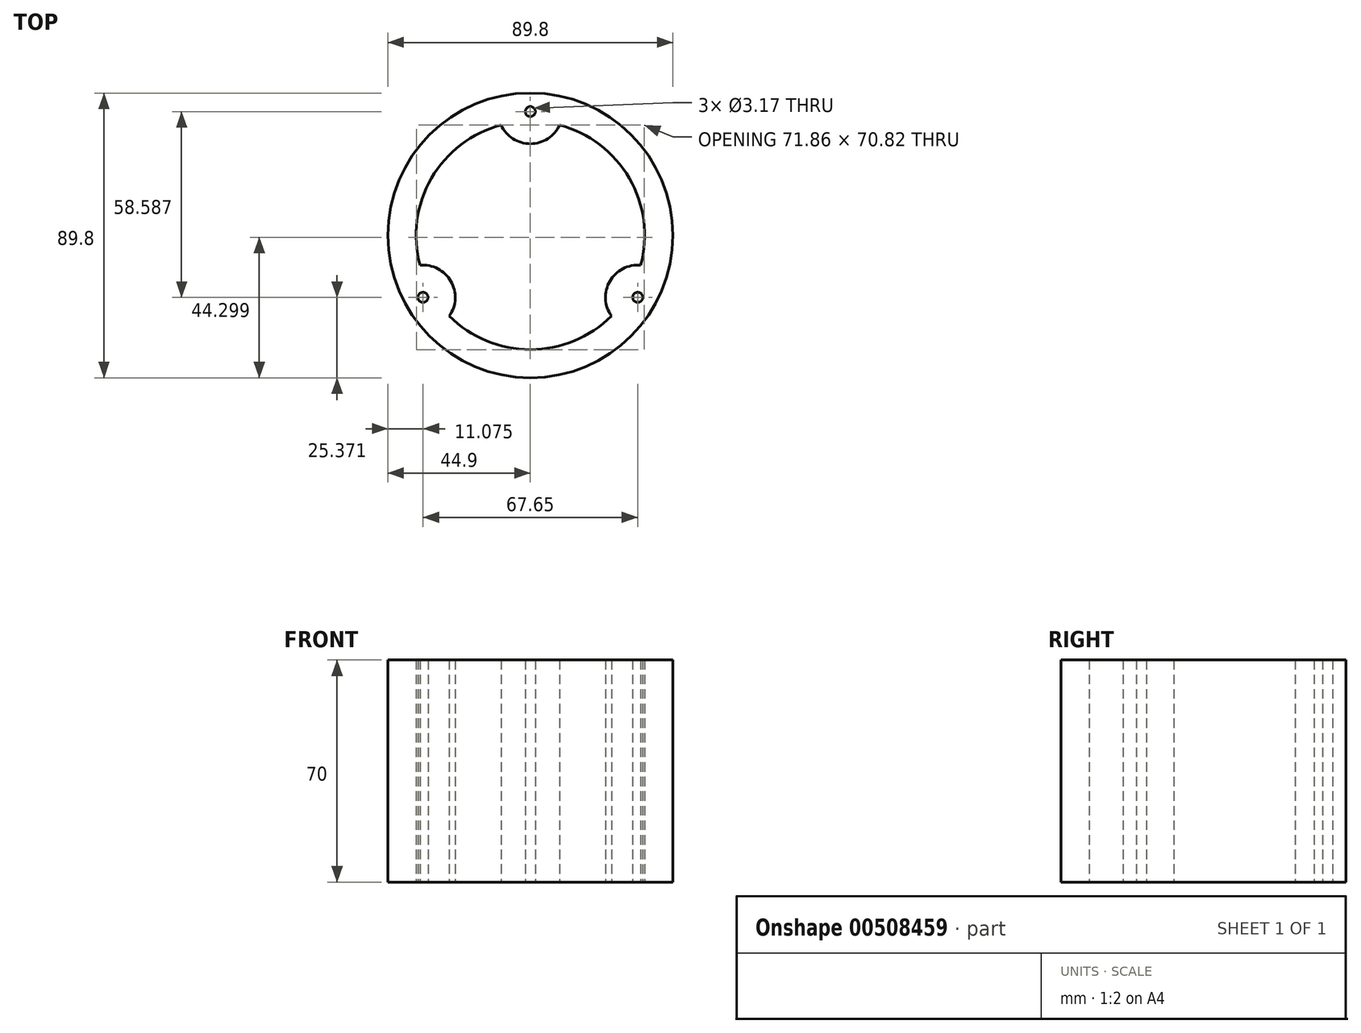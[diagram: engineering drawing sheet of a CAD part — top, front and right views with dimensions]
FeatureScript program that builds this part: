
annotation { "Feature Type Name" : "Feature", "Feature Type Description" : "" }
export const myFeature = defineFeature(function(context is Context, id is Id, definition is map)
    precondition{}
    {
        {
            var Q0;
            Q0=qCreatedBy(makeId("Top.planeOp"),FACE);
            var sketch = newSketch(context, id + "F0", { "sketchPlane" : qUnion([Q0])});
            skCircle(sketch, "E0", {"center": v(0, 0) * mm, "radius": 44.9 * mm});
            skCircle(sketch, "E1", {"center": v(0, 0) * mm, "radius": 36 * mm});
            skPoint(sketch, "E2", {"position": v(0, 39.06) * mm});
            skPoint(sketch, "E3.1.0", {"position": v(-33.83, -19.53) * mm});
            skPoint(sketch, "E3.2.0", {"position": v(33.83, -19.53) * mm});
            skCircle(sketch, "E4", {"center": v(0, 39.06) * mm, "radius": 1.59 * mm});
            skCircle(sketch, "E5", {"center": v(33.83, -19.53) * mm, "radius": 1.59 * mm});
            skCircle(sketch, "E6", {"center": v(-33.83, -19.53) * mm, "radius": 1.59 * mm});
            skCircle(sketch, "E7", {"center": v(0, 39.06) * mm, "radius": 10.16 * mm});
            skCircle(sketch, "E8.1.0", {"center": v(-33.83, -19.53) * mm, "radius": 10.16 * mm});
            skCircle(sketch, "E8.2.0", {"center": v(33.83, -19.53) * mm, "radius": 10.16 * mm});
            skSolve(sketch);
        }
        {
            var Q0;
            Q0=makeQuery(id+"F0.imprint","IMPRINT",FACE,{"disambiguationData":[TD([[makeQuery(id+"F0.imprint","IMPRINT",EDGE,{"derivedFrom":sQuery(id+"F0.wireOp",EDGE,"E6")}),-1.0]])]});
            var Q1;
            {var subQ0=sQuery(id+"F0.wireOp",EDGE,"E8.1.0");var subQ1=sQuery(id+"F0.wireOp",EDGE,"E0");var subQ2=makeQuery(id+"F0.imprint","INTERSECT",VERTEX,{"disambiguationData":[OD(1.0)],"derivedFrom":[subQ1,subQ0]});Q1=makeQuery(id+"F0.imprint","IMPRINT",FACE,{"disambiguationData":[TD([[makeQuery(id+"F0.imprint","IMPRINT",EDGE,{"disambiguationData":[TD([[subQ2,-1.0]])],"derivedFrom":subQ1}),1.0]])]});}
            var Q2;
            Q2=makeQuery(id+"F0.imprint","IMPRINT",FACE,{"disambiguationData":[TD([[makeQuery(id+"F0.imprint","IMPRINT",EDGE,{"derivedFrom":sQuery(id+"F0.wireOp",EDGE,"E5")}),-1.0]])]});
            var Q3;
            {var subQ0=sQuery(id+"F0.wireOp",EDGE,"E8.2.0");var subQ1=sQuery(id+"F0.wireOp",EDGE,"E1");var subQ2=makeQuery(id+"F0.imprint","INTERSECT",VERTEX,{"disambiguationData":[OD(0.0)],"derivedFrom":[subQ1,subQ0]});Q3=makeQuery(id+"F0.imprint","IMPRINT",FACE,{"disambiguationData":[TD([[makeQuery(id+"F0.imprint","IMPRINT",EDGE,{"disambiguationData":[TD([[subQ2,-1.0]])],"derivedFrom":subQ1}),1.0]])]});}
            var Q4;
            {var subQ0=sQuery(id+"F0.wireOp",EDGE,"E8.1.0");var subQ1=sQuery(id+"F0.wireOp",EDGE,"E1");var subQ2=makeQuery(id+"F0.imprint","INTERSECT",VERTEX,{"disambiguationData":[OD(0.0)],"derivedFrom":[subQ1,subQ0]});Q4=makeQuery(id+"F0.imprint","IMPRINT",FACE,{"disambiguationData":[TD([[makeQuery(id+"F0.imprint","IMPRINT",EDGE,{"disambiguationData":[TD([[subQ2,-1.0]])],"derivedFrom":subQ1}),1.0]])]});}
            var Q5;
            {var subQ0=sQuery(id+"F0.wireOp",EDGE,"E7");var subQ1=sQuery(id+"F0.wireOp",EDGE,"E0");var subQ2=makeQuery(id+"F0.imprint","INTERSECT",VERTEX,{"disambiguationData":[OD(0.0)],"derivedFrom":[subQ1,subQ0]});Q5=makeQuery(id+"F0.imprint","IMPRINT",FACE,{"disambiguationData":[TD([[makeQuery(id+"F0.imprint","IMPRINT",EDGE,{"disambiguationData":[TD([[subQ2,-1.0]])],"derivedFrom":subQ1}),1.0]])]});}
            var Q6;
            Q6=makeQuery(id+"F0.imprint","IMPRINT",FACE,{"disambiguationData":[TD([[makeQuery(id+"F0.imprint","IMPRINT",EDGE,{"derivedFrom":sQuery(id+"F0.wireOp",EDGE,"E4")}),-1.0]])]});
            var Q7;
            {var subQ0=sQuery(id+"F0.wireOp",EDGE,"E7");var subQ1=sQuery(id+"F0.wireOp",EDGE,"E1");var subQ2=makeQuery(id+"F0.imprint","INTERSECT",VERTEX,{"disambiguationData":[OD(0.0)],"derivedFrom":[subQ1,subQ0]});Q7=makeQuery(id+"F0.imprint","IMPRINT",FACE,{"disambiguationData":[TD([[makeQuery(id+"F0.imprint","IMPRINT",EDGE,{"disambiguationData":[TD([[subQ2,1.0]])],"derivedFrom":subQ1}),1.0]])]});}
            var Q8;
            {var subQ0=sQuery(id+"F0.wireOp",EDGE,"E7");var subQ1=sQuery(id+"F0.wireOp",EDGE,"E0");var subQ2=makeQuery(id+"F0.imprint","INTERSECT",VERTEX,{"disambiguationData":[OD(1.0)],"derivedFrom":[subQ1,subQ0]});Q8=makeQuery(id+"F0.imprint","IMPRINT",FACE,{"disambiguationData":[TD([[makeQuery(id+"F0.imprint","IMPRINT",EDGE,{"disambiguationData":[TD([[subQ2,1.0]])],"derivedFrom":subQ1}),1.0]])]});}
            extrude(context, id + "F1", {"entities" : qUnion([Q0, Q1, Q2, Q3, Q4, Q5, Q6, Q7, Q8]), "depth" : 70 * mm});
        }
    });
